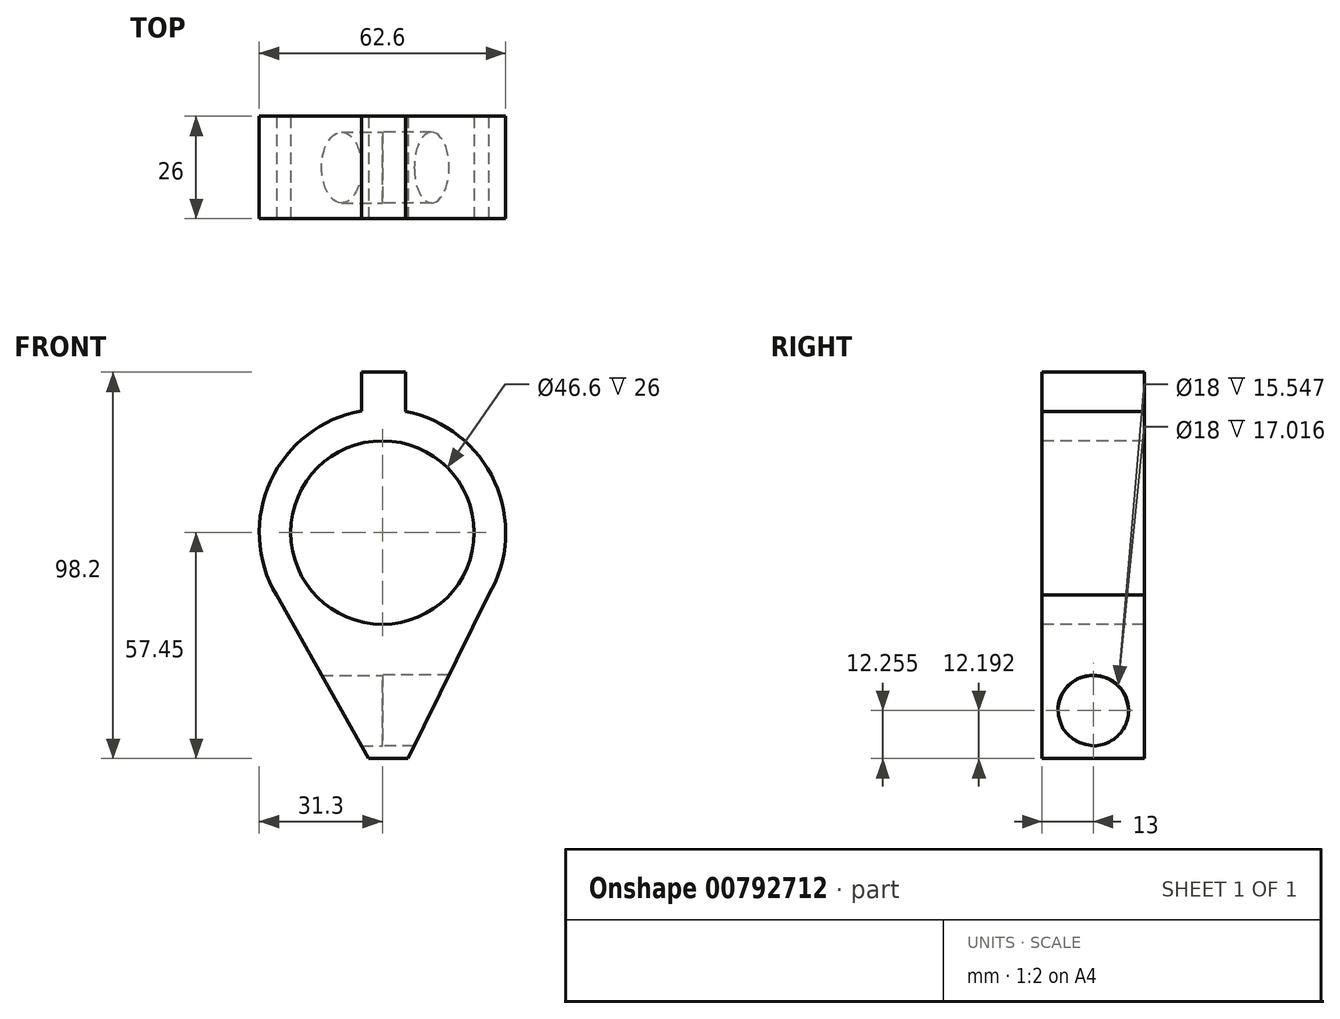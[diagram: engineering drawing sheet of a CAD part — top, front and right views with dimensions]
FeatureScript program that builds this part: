
annotation { "Feature Type Name" : "Feature", "Feature Type Description" : "" }
export const myFeature = defineFeature(function(context is Context, id is Id, definition is map)
    precondition{}
    {
        {
            var Q0;
            Q0=qCreatedBy(makeId("Front.planeOp"),FACE);
            var sketch = newSketch(context, id + "F0", { "sketchPlane" : qUnion([Q0])});
            skCircle(sketch, "E0", {"center": v(0, 0) * mm, "radius": 23.3 * mm});
            skCircle(sketch, "E1", {"center": v(0, 0) * mm, "radius": 31.3 * mm});
            skLineSegment(sketch, "E2", {"start": v(-3.52, -57.45) * mm, "end": v(6.48, -57.45) * mm});
            skLineSegment(sketch, "E3", {"start": v(-26.95, -15.92) * mm, "end": v(-3.52, -57.45) * mm});
            skLineSegment(sketch, "E4", {"start": v(26.95, -15.92) * mm, "end": v(6.48, -57.45) * mm});
            skLineSegment(sketch, "E5", {"start": v(-5.34, 30.84) * mm, "end": v(-5.34, 40.75) * mm});
            skLineSegment(sketch, "E6", {"start": v(-5.34, 40.75) * mm, "end": v(5.88, 40.75) * mm});
            skLineSegment(sketch, "E7", {"start": v(5.88, 40.75) * mm, "end": v(5.88, 30.74) * mm});
            skLineSegment(sketch, "E8", {"start": v(1.48, -57.45) * mm, "end": v(1.48, -31.27) * mm});
            skSolve(sketch);
        }
        {
            var Q0;
            Q0=qCreatedBy(makeId("Right.planeOp"),FACE);
            var sketch = newSketch(context, id + "F1", { "sketchPlane" : qUnion([Q0])});
            skCircle(sketch, "E9", {"center": v(13, -45.26) * mm, "radius": 9 * mm});
            skLineSegment(sketch, "E10", {"start": v(0, -58.26) * mm, "end": v(26, -58.26) * mm});
            skLineSegment(sketch, "E11", {"start": v(26, -58.26) * mm, "end": v(26, 0) * mm});
            skArc(sketch, "E12", {"start": v(0, -45.07) * mm, "mid": v(12.94, -58.2) * mm, "end": v(26, -45.2) * mm});
            skSolve(sketch);
        }
        {
            var Q0;
            {var subQ0=sQuery(id+"F0.wireOp",EDGE,"E5");Q0=makeQuery(id+"F0.imprint","IMPRINT",FACE,{"disambiguationData":[TD([[makeQuery(id+"F0.imprint","IMPRINT",EDGE,{"derivedFrom":subQ0}),-1.0]])]});}
            var Q1;
            Q1=makeQuery(id+"F0.imprint","IMPRINT",FACE,{"disambiguationData":[TD([[makeQuery(id+"F0.imprint","IMPRINT",EDGE,{"derivedFrom":sQuery(id+"F0.wireOp",EDGE,"E0")}),-1.0]])]});
            var Q2;
            {var subQ0=sQuery(id+"F0.wireOp",EDGE,"E4");Q2=makeQuery(id+"F0.imprint","IMPRINT",FACE,{"disambiguationData":[TD([[makeQuery(id+"F0.imprint","IMPRINT",EDGE,{"derivedFrom":subQ0}),-1.0]])]});}
            var Q3;
            {var subQ0=sQuery(id+"F0.wireOp",EDGE,"E3");Q3=makeQuery(id+"F0.imprint","IMPRINT",FACE,{"disambiguationData":[TD([[makeQuery(id+"F0.imprint","IMPRINT",EDGE,{"derivedFrom":subQ0}),1.0]])]});}
            extrude(context, id + "F2", {"entities" : qUnion([Q0, Q1, Q2, Q3]), "oppositeDirection" : true, "depth" : 26 * mm, "offsetDistance" : 25 * mm});
        }
        {
            var Q0;
            Q0=sQuery(id+"F1.wireOp",VERTEX,"E9.center");
            var Q1;
            Q1=makeQuery(id+"F2.opExtrude","SWEPT_BODY",BODY,{"disambiguationData":[OSD([sQuery(id+"F0.wireOp",EDGE,"E0"),sQuery(id+"F0.wireOp",EDGE,"E1"),sQuery(id+"F0.wireOp",EDGE,"E2"),sQuery(id+"F0.wireOp",EDGE,"E3"),sQuery(id+"F0.wireOp",EDGE,"E4"),sQuery(id+"F0.wireOp",EDGE,"E5"),sQuery(id+"F0.wireOp",EDGE,"E6"),sQuery(id+"F0.wireOp",EDGE,"E7")])]});
            hole(context, id + "F3", {"style" : HoleStyle.SIMPLE, "endStyle" : HoleEndStyle.THROUGH, "holeDiameter" : 18 * mm, "majorDiameter" : 5 * mm, "isTappedThrough" : true, "tappedDepth" : 12 * mm, "tapClearance" : 3, "locations" : qUnion([Q0]), "scope" : qUnion([Q1])});
        }
        {
            var Q0;
            Q0=sQuery(id+"F1.wireOp",VERTEX,"E12.center");
            var Q1;
            Q1=makeQuery(id+"F2.opExtrude","SWEPT_BODY",BODY,{"disambiguationData":[OSD([sQuery(id+"F0.wireOp",EDGE,"E0"),sQuery(id+"F0.wireOp",EDGE,"E1"),sQuery(id+"F0.wireOp",EDGE,"E2"),sQuery(id+"F0.wireOp",EDGE,"E3"),sQuery(id+"F0.wireOp",EDGE,"E4"),sQuery(id+"F0.wireOp",EDGE,"E5"),sQuery(id+"F0.wireOp",EDGE,"E6"),sQuery(id+"F0.wireOp",EDGE,"E7")])]});
            hole(context, id + "F4", {"style" : HoleStyle.SIMPLE, "endStyle" : HoleEndStyle.THROUGH, "oppositeDirection" : true, "holeDiameter" : 18 * mm, "majorDiameter" : 5 * mm, "isTappedThrough" : true, "tappedDepth" : 12 * mm, "tapClearance" : 3, "locations" : qUnion([Q0]), "scope" : qUnion([Q1])});
        }
    });
